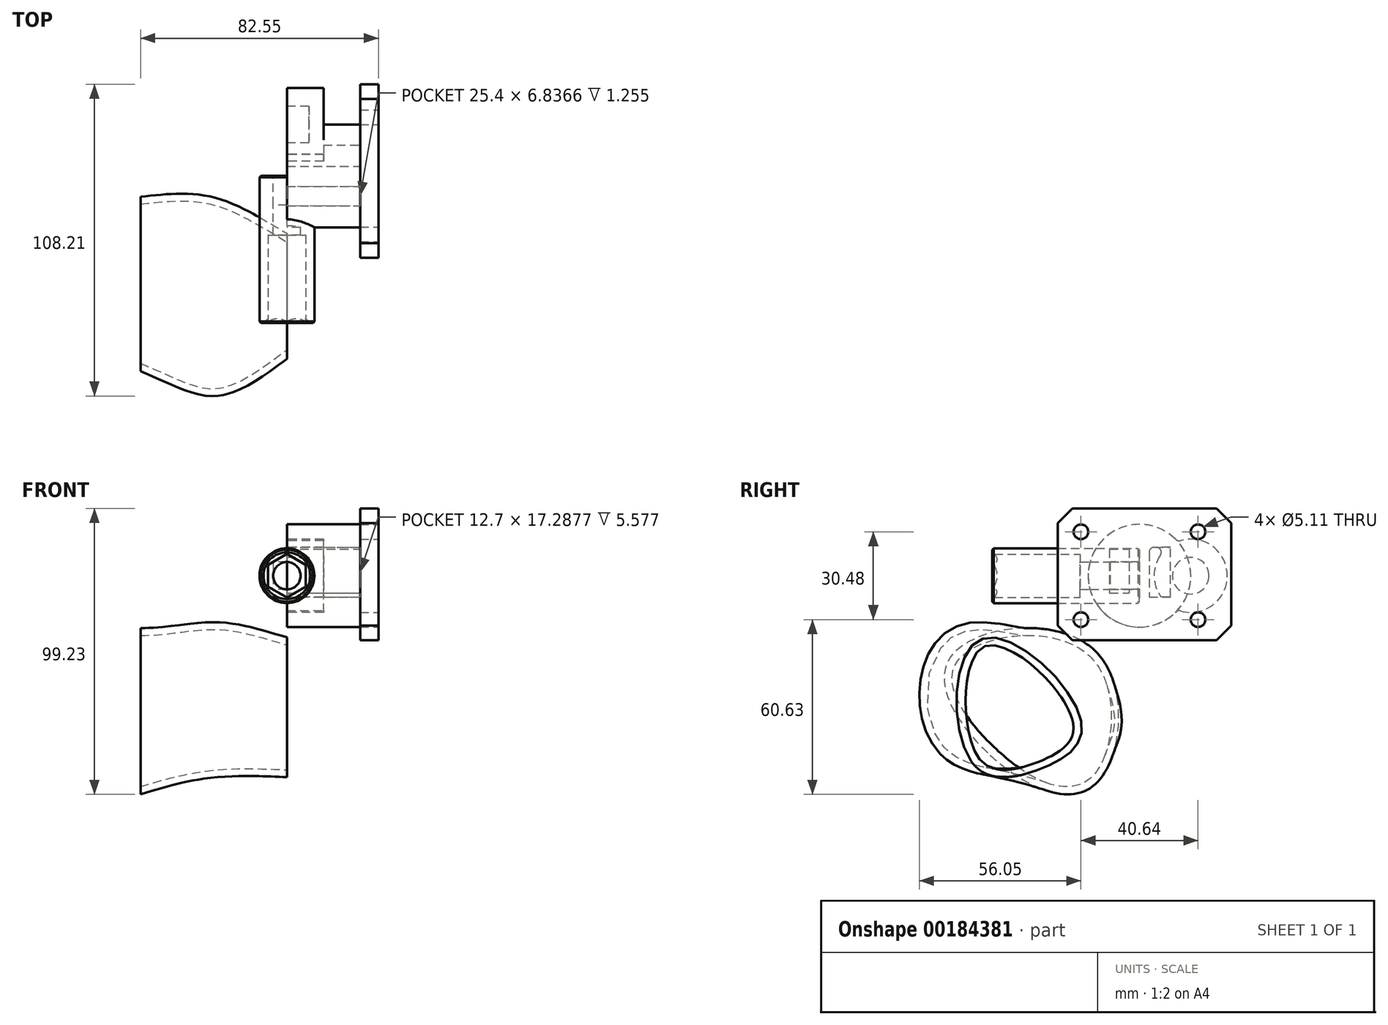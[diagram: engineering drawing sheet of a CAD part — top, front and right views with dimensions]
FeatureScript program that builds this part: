
annotation { "Feature Type Name" : "Feature", "Feature Type Description" : "" }
export const myFeature = defineFeature(function(context is Context, id is Id, definition is map)
    precondition{}
    {
        {
            var Q0;
            Q0=qCreatedBy(makeId("Front.planeOp"),FACE);
            var sketch = newSketch(context, id + "F0", { "sketchPlane" : qUnion([Q0])});
            skCircle(sketch, "E0", {"center": v(0, 0) * mm, "radius": 9.53 * mm});
            skSolve(sketch);
        }
        {
            var Q0;
            Q0 = qSketchRegion(id + "F0", true);
            extrude(context, id + "F1", {"entities" : qUnion([Q0]), "depth" : 51.05 * mm});
        }
        {
            var Q0;
            Q0=qCreatedBy(makeId("Front.planeOp"),FACE);
            var sketch = newSketch(context, id + "F2", { "sketchPlane" : qUnion([Q0])});
            skLineSegment(sketch, "E1.bottom", {"start": v(4.76, 4.76) * mm, "end": v(-4.76, 4.76) * mm});
            skLineSegment(sketch, "E1.top", {"start": v(4.76, -4.76) * mm, "end": v(-4.76, -4.76) * mm});
            skLineSegment(sketch, "E1.left", {"start": v(4.76, 4.76) * mm, "end": v(4.76, -4.76) * mm});
            skLineSegment(sketch, "E1.right", {"start": v(-4.76, 4.76) * mm, "end": v(-4.76, -4.76) * mm});
            skPoint(sketch, "E1.middle", {"position": v(0, 0) * mm});
            skCircle(sketch, "E2", {"center": v(0, 0) * mm, "radius": 4.76 * mm});
            skSolve(sketch);
        }
        {
            var Q0;
            {var subQ0=sQuery(id+"F2.wireOp",EDGE,"E2");var subQ1=makeQuery(id+"F2.imprint","INTERSECT",VERTEX,{"derivedFrom":[sQuery(id+"F2.wireOp",EDGE,"E1.bottom"),subQ0]});Q0=makeQuery(id+"F2.imprint","IMPRINT",FACE,{"disambiguationData":[TD([[makeQuery(id+"F2.imprint","IMPRINT",EDGE,{"disambiguationData":[TD([[subQ1,1.0]])],"derivedFrom":subQ0}),1.0]])]});}
            extrude(context, id + "F3", {"entities" : qUnion([Q0]), "operationType" : NewBodyOperationType.REMOVE, "endBound" : BoundingType.THROUGH_ALL, "depth" : 25.4 * mm});
        }
        {
            var Q0;
            Q0 = qSketchRegion(id + "F2", true);
            extrude(context, id + "F4", {"entities" : qUnion([Q0]), "operationType" : NewBodyOperationType.REMOVE, "depth" : 10.16 * mm});
        }
        {
            var Q0;
            Q0=makeQuery(id+"F1.opExtrude","CAP_FACE",FACE,{"disambiguationData":[OSD([sQuery(id+"F0.wireOp",EDGE,"E0")])],"isStart":false});
            var sketch = newSketch(context, id + "F5", { "sketchPlane" : qUnion([Q0])});
            skCircle(sketch, "E3.cCircle", {"center": v(0, 0) * mm, "radius": 6.54 * mm, "construction": true});
            skLineSegment(sketch, "E3.0", {"start": v(6.54, 3.78) * mm, "end": v(6.54, -3.78) * mm});
            skLineSegment(sketch, "E3.1", {"start": v(6.54, -3.78) * mm, "end": v(0, -7.55) * mm});
            skLineSegment(sketch, "E3.2", {"start": v(0, -7.55) * mm, "end": v(-6.54, -3.78) * mm});
            skLineSegment(sketch, "E3.3", {"start": v(-6.54, -3.78) * mm, "end": v(-6.54, 3.78) * mm});
            skLineSegment(sketch, "E3.4", {"start": v(-6.54, 3.78) * mm, "end": v(0, 7.55) * mm});
            skLineSegment(sketch, "E3.5", {"start": v(0, 7.55) * mm, "end": v(6.54, 3.78) * mm});
            skPoint(sketch, "E3.0.midPoint", {"position": v(6.54, 0) * mm});
            skSolve(sketch);
        }
        {
            var Q0;
            Q0 = qSketchRegion(id + "F5", true);
            extrude(context, id + "F6", {"entities" : qUnion([Q0]), "operationType" : NewBodyOperationType.REMOVE, "oppositeDirection" : true, "depth" : 30.48 * mm});
        }
        {
            var Q0;
            Q0=makeQuery(id+"F6.boolean.opBoolean","COPY",EDGE,{"derivedFrom":makeQuery(id+"F6.opExtrude","SWEPT_EDGE",EDGE,{"disambiguationData":[OSD([sQuery(id+"F5.wireOp",EDGE,"E3.4"),sQuery(id+"F5.wireOp",EDGE,"E3.5")])]})});
            var Q1;
            Q1=makeQuery(id+"F6.boolean.opBoolean","COPY",EDGE,{"derivedFrom":makeQuery(id+"F6.opExtrude","SWEPT_EDGE",EDGE,{"disambiguationData":[OSD([sQuery(id+"F5.wireOp",EDGE,"E3.3"),sQuery(id+"F5.wireOp",EDGE,"E3.4")])]})});
            var Q2;
            Q2=makeQuery(id+"F6.boolean.opBoolean","COPY",EDGE,{"derivedFrom":makeQuery(id+"F6.opExtrude","SWEPT_EDGE",EDGE,{"disambiguationData":[OSD([sQuery(id+"F5.wireOp",EDGE,"E3.2"),sQuery(id+"F5.wireOp",EDGE,"E3.3")])]})});
            var Q3;
            Q3=makeQuery(id+"F6.boolean.opBoolean","COPY",EDGE,{"derivedFrom":makeQuery(id+"F6.opExtrude","SWEPT_EDGE",EDGE,{"disambiguationData":[OSD([sQuery(id+"F5.wireOp",EDGE,"E3.1"),sQuery(id+"F5.wireOp",EDGE,"E3.2")])]})});
            var Q4;
            Q4=makeQuery(id+"F6.boolean.opBoolean","COPY",EDGE,{"derivedFrom":makeQuery(id+"F6.opExtrude","SWEPT_EDGE",EDGE,{"disambiguationData":[OSD([sQuery(id+"F5.wireOp",EDGE,"E3.0"),sQuery(id+"F5.wireOp",EDGE,"E3.1")])]})});
            var Q5;
            Q5=makeQuery(id+"F6.boolean.opBoolean","COPY",EDGE,{"derivedFrom":makeQuery(id+"F6.opExtrude","SWEPT_EDGE",EDGE,{"disambiguationData":[OSD([sQuery(id+"F5.wireOp",EDGE,"E3.0"),sQuery(id+"F5.wireOp",EDGE,"E3.5")])]})});
            fillet(context, id + "F7", {"entities" : qUnion([Q0, Q1, Q2, Q3, Q4, Q5]), "radius" : 0.5 * mm, "tangentPropagation" : true, "allowEdgeOverflow" : false});
        }
        {
            var Q0;
            Q0=qCreatedBy(makeId("Right.planeOp"),FACE);
            var sketch = newSketch(context, id + "F8", { "sketchPlane" : qUnion([Q0])});
            skLineSegment(sketch, "E4", {"start": v(0, 0) * mm, "end": v(-83.35, 0) * mm, "construction": true});
            skLineSegment(sketch, "E5", {"start": v(-51.05, 8.13) * mm, "end": v(-42.93, 0) * mm});
            skLineSegment(sketch, "E6", {"start": v(-42.93, 0) * mm, "end": v(-51.05, 0) * mm});
            skLineSegment(sketch, "E7", {"start": v(-51.05, 0) * mm, "end": v(-51.05, 8.13) * mm});
            skSolve(sketch);
        }
        {
            var Q0;
            Q0=makeQuery(id+"F8.imprint","IMPRINT",FACE,{"disambiguationData":[TD([[makeQuery(id+"F8.imprint","IMPRINT",EDGE,{"derivedFrom":sQuery(id+"F8.wireOp",EDGE,"E5")}),-1.0]])]});
            var Q1;
            Q1=sQuery(id+"F8.wireOp",EDGE,"E4");
            revolve(context, id + "F9", {"operationType" : NewBodyOperationType.REMOVE, "entities" : qUnion([Q0]), "axis" : qUnion([Q1]), "revolveType" : RevolveType.FULL, "oppositeDirection" : true});
        }
        {
            var Q0;
            Q0=makeQuery(id+"F1.opExtrude","CAP_EDGE",EDGE,{"disambiguationData":[OSD([sQuery(id+"F0.wireOp",EDGE,"E0")])],"isStart":false});
            var Q1;
            Q1=makeQuery(id+"F1.opExtrude","CAP_EDGE",EDGE,{"disambiguationData":[OSD([sQuery(id+"F0.wireOp",EDGE,"E0")])],"isStart":true});
            chamfer(context, id + "F10", {"entities" : qUnion([Q0, Q1]), "width" : 0.5 * mm, "tangentPropagation" : true});
        }
        {
            var Q0;
            Q0=qCreatedBy(makeId("Right.planeOp"),FACE);
            var sketch = newSketch(context, id + "F11", { "sketchPlane" : qUnion([Q0])});
            skCircle(sketch, "E8", {"center": v(0, 0) * mm, "radius": 17.82 * mm});
            skSolve(sketch);
        }
        {
            var Q0;
            Q0 = qSketchRegion(id + "F11", true);
            extrude(context, id + "F12", {"entities" : qUnion([Q0]), "operationType" : NewBodyOperationType.ADD, "depth" : 25.4 * mm});
        }
        {
            var Q0;
            Q0=makeQuery(id+"F12.opExtrude","CAP_FACE",FACE,{"disambiguationData":[OSD([sQuery(id+"F11.wireOp",EDGE,"E8")])],"isStart":false});
            var sketch = newSketch(context, id + "F13", { "sketchPlane" : qUnion([Q0])});
            skLineSegment(sketch, "E9.bottom", {"start": v(-10.41, 9.23) * mm, "end": v(-3.58, 9.23) * mm});
            skLineSegment(sketch, "E9.top", {"start": v(-10.41, -6.02) * mm, "end": v(-3.58, -6.02) * mm});
            skLineSegment(sketch, "E9.left", {"start": v(-10.41, 9.23) * mm, "end": v(-10.41, -6.02) * mm});
            skLineSegment(sketch, "E9.right", {"start": v(-3.58, 9.23) * mm, "end": v(-3.58, -6.02) * mm});
            skLineSegment(sketch, "E10.bottom", {"start": v(3.37, 9.89) * mm, "end": v(10.73, 9.89) * mm});
            skLineSegment(sketch, "E10.top", {"start": v(3.37, -7.4) * mm, "end": v(10.73, -7.4) * mm});
            skLineSegment(sketch, "E10.left", {"start": v(3.37, 9.89) * mm, "end": v(3.37, -7.4) * mm});
            skLineSegment(sketch, "E10.right", {"start": v(10.73, 9.89) * mm, "end": v(10.73, -7.4) * mm});
            skSolve(sketch);
        }
        {
            var Q0;
            Q0 = qSketchRegion(id + "F13", true);
            extrude(context, id + "F14", {"entities" : qUnion([Q0]), "operationType" : NewBodyOperationType.REMOVE, "oppositeDirection" : true, "depth" : 25.4 * mm});
        }
        {
            var Q0;
            Q0=makeQuery(id+"F12.opExtrude","CAP_FACE",FACE,{"disambiguationData":[OSD([sQuery(id+"F11.wireOp",EDGE,"E8")])],"isStart":false});
            var sketch = newSketch(context, id + "F15", { "sketchPlane" : qUnion([Q0])});
            skLineSegment(sketch, "E11.bottom", {"start": v(-28.4, 23.36) * mm, "end": v(31.84, 23.36) * mm});
            skLineSegment(sketch, "E11.top", {"start": v(-28.4, -22.4) * mm, "end": v(31.84, -22.4) * mm});
            skLineSegment(sketch, "E11.left", {"start": v(-28.4, 23.36) * mm, "end": v(-28.4, -22.4) * mm});
            skLineSegment(sketch, "E11.right", {"start": v(31.84, 23.36) * mm, "end": v(31.84, -22.4) * mm});
            skSolve(sketch);
        }
        {
            var Q0;
            Q0 = qSketchRegion(id + "F15", true);
            extrude(context, id + "F16", {"entities" : qUnion([Q0]), "operationType" : NewBodyOperationType.ADD, "depth" : 6.35 * mm});
        }
        {
            var Q0;
            Q0=qCreatedBy(makeId("Right.planeOp"),FACE);
            var sketch = newSketch(context, id + "F17", { "sketchPlane" : qUnion([Q0])});
            skCircle(sketch, "E12", {"center": v(17.78, 0) * mm, "radius": 12.7 * mm});
            skSolve(sketch);
        }
        {
            var Q0;
            Q0 = qSketchRegion(id + "F17", true);
            extrude(context, id + "F18", {"entities" : qUnion([Q0]), "operationType" : NewBodyOperationType.ADD, "depth" : 12.7 * mm});
        }
        {
            var Q0;
            Q0=makeQuery(id+"F16.opExtrude","SWEPT_EDGE",EDGE,{"disambiguationData":[OSD([sQuery(id+"F15.wireOp",EDGE,"E11.top"),sQuery(id+"F15.wireOp",EDGE,"E11.right")])]});
            var Q1;
            Q1=makeQuery(id+"F16.opExtrude","SWEPT_EDGE",EDGE,{"disambiguationData":[OSD([sQuery(id+"F15.wireOp",EDGE,"E11.top"),sQuery(id+"F15.wireOp",EDGE,"E11.left")])]});
            var Q2;
            Q2=makeQuery(id+"F16.opExtrude","SWEPT_EDGE",EDGE,{"disambiguationData":[OSD([sQuery(id+"F15.wireOp",EDGE,"E11.bottom"),sQuery(id+"F15.wireOp",EDGE,"E11.left")])]});
            var Q3;
            Q3=makeQuery(id+"F16.opExtrude","SWEPT_EDGE",EDGE,{"disambiguationData":[OSD([sQuery(id+"F15.wireOp",EDGE,"E11.bottom"),sQuery(id+"F15.wireOp",EDGE,"E11.right")])]});
            chamfer(context, id + "F19", {"entities" : qUnion([Q0, Q1, Q2, Q3]), "width" : 5.08 * mm, "tangentPropagation" : true});
        }
        {
            var Q0;
            Q0=makeQuery(id+"F16.opExtrude","CAP_FACE",FACE,{"disambiguationData":[OSD([sQuery(id+"F15.wireOp",EDGE,"E11.bottom"),sQuery(id+"F15.wireOp",EDGE,"E11.top"),sQuery(id+"F15.wireOp",EDGE,"E11.left"),sQuery(id+"F15.wireOp",EDGE,"E11.right")])],"isStart":false});
            var sketch = newSketch(context, id + "F20", { "sketchPlane" : qUnion([Q0])});
            skCircle(sketch, "E13", {"center": v(-20.32, -15.24) * mm, "radius": 2.55 * mm});
            skLineSegment(sketch, "E14", {"start": v(0, 0) * mm, "end": v(-58.83, 0) * mm, "construction": true});
            skCircle(sketch, "E15.MirrorC", {"center": v(-20.32, 15.24) * mm, "radius": 2.55 * mm});
            skLineSegment(sketch, "E16", {"start": v(0, 0) * mm, "end": v(0, -86.74) * mm, "construction": true});
            skCircle(sketch, "E17.MirrorC", {"center": v(20.32, 15.24) * mm, "radius": 2.55 * mm});
            skCircle(sketch, "E18.MirrorC", {"center": v(20.32, -15.24) * mm, "radius": 2.55 * mm});
            skSolve(sketch);
        }
        {
            var Q0;
            Q0 = qSketchRegion(id + "F20", true);
            extrude(context, id + "F21", {"entities" : qUnion([Q0]), "operationType" : NewBodyOperationType.REMOVE, "oppositeDirection" : true, "depth" : 12.7 * mm});
        }
        {
            var Q0;
            Q0=qCreatedBy(makeId("Right.planeOp"),FACE);
            var sketch = newSketch(context, id + "F22", { "sketchPlane" : qUnion([Q0])});
            skFitSpline(sketch, "E19", {"points": [v(-58.52, -64.24) * mm, v(-33.89, -66.86) * mm, v(-20.22, -50.28) * mm, v(-54.96, -22.02) * mm, v(-58.52, -64.24) * mm]});
            skSolve(sketch);
        }
        {
            var Q0;
            Q0=qCreatedBy(makeId("Right.planeOp"),FACE);
            cPlane(context, id + "F23", {"entities" : qUnion([Q0]), "cplaneType" : CPlaneType.OFFSET, "offset" : 25.4 * mm, "oppositeDirection" : true, "width" : 152.4 * mm, "height" : 152.4 * mm});
        }
        {
            var Q0;
            Q0=qCreatedBy(id+"F23.planeOp",FACE);
            var sketch = newSketch(context, id + "F24", { "sketchPlane" : qUnion([Q0])});
            skFitSpline(sketch, "E20", {"points": [v(-12.92, -61.32) * mm, v(-13.1, -37.85) * mm, v(-65.5, -18.56) * mm, v(-68.96, -61.68) * mm, v(-12.92, -61.32) * mm]});
            skSolve(sketch);
        }
        {
            var Q0;
            Q0=qCreatedBy(id+"F23.planeOp",FACE);
            cPlane(context, id + "F25", {"entities" : qUnion([Q0]), "cplaneType" : CPlaneType.OFFSET, "offset" : 25.4 * mm, "oppositeDirection" : true, "width" : 152.4 * mm, "height" : 152.4 * mm});
        }
        {
            var Q0;
            Q0=qCreatedBy(id+"F25.planeOp",FACE);
            var sketch = newSketch(context, id + "F26", { "sketchPlane" : qUnion([Q0])});
            skFitSpline(sketch, "E21", {"points": [v(-15.83, -72.78) * mm, v(-15.65, -25.84) * mm, v(-65.32, -27.84) * mm, v(-51.86, -62.23) * mm, v(-15.83, -72.78) * mm]});
            skSolve(sketch);
        }
        {
            var Q0;
            Q0=makeQuery(id+"F22.imprint","IMPRINT",FACE,{"disambiguationData":[TD([[makeQuery(id+"F22.imprint","IMPRINT",EDGE,{"derivedFrom":sQuery(id+"F22.wireOp",EDGE,"E19")}),1.0]])]});
            var Q1;
            Q1=makeQuery(id+"F24.imprint","IMPRINT",FACE,{"disambiguationData":[TD([[makeQuery(id+"F24.imprint","IMPRINT",EDGE,{"derivedFrom":sQuery(id+"F24.wireOp",EDGE,"E20")}),1.0]])]});
            var Q2;
            Q2=makeQuery(id+"F26.imprint","IMPRINT",FACE,{"disambiguationData":[TD([[makeQuery(id+"F26.imprint","IMPRINT",EDGE,{"derivedFrom":sQuery(id+"F26.wireOp",EDGE,"E21")}),1.0]])]});
            var Q3;
            Q3=sQuery(id+"F22.wireOp",VERTEX,"E19.0.internal");
            var Q4;
            Q4=sQuery(id+"F24.wireOp",VERTEX,"E20.3.internal");
            var Q5;
            Q5=sQuery(id+"F26.wireOp",VERTEX,"E21.3.internal");
            loft(context, id + "F27", {"sheetProfilesArray" : [{ "sheetProfileEntities" : qUnion([Q0]) }, { "sheetProfileEntities" : qUnion([Q1]) }, { "sheetProfileEntities" : qUnion([Q2]) }], "matchConnections" : true, "connections" : [{ "connectionEntities" : qUnion([Q3, Q4, Q5]), "connectionEdgeQueries" : qUnion([]), "connectionEdgeParameters" : [] }]});
        }
        {
            var Q0;
            {var subQ1=sQuery(id+"F11.wireOp",EDGE,"E8");var subQ2=sQuery(id+"F0.wireOp",EDGE,"E0");Q0=makeQuery(id+"F18.boolean.opBoolean","MERGE",FACE,{"derivedFrom":[makeQuery(id+"F14.boolean.opBoolean","SPLIT",FACE,{"disambiguationData":[TD([makeQuery(id+"F1.opExtrude","SWEPT_FACE",FACE,{"disambiguationData":[OSD([subQ2])]})])],"derivedFrom":makeQuery(id+"F12.opExtrude","CAP_FACE",FACE,{"disambiguationData":[OSD([subQ1])],"isStart":true})}),makeQuery(id+"F18.opExtrude","CAP_FACE",FACE,{"disambiguationData":[OSD([sQuery(id+"F17.wireOp",EDGE,"E12")])],"isStart":true})]});}
            var sketch = newSketch(context, id + "F28", { "sketchPlane" : qUnion([Q0])});
            skCircle(sketch, "E22", {"center": v(-17.78, 0) * mm, "radius": 6.35 * mm});
            skSolve(sketch);
        }
        {
            var Q0;
            Q0 = qSketchRegion(id + "F28", true);
            extrude(context, id + "F29", {"entities" : qUnion([Q0]), "operationType" : NewBodyOperationType.REMOVE, "oppositeDirection" : true, "depth" : 7.62 * mm});
        }
        {
            var Q0;
            {var subQ0=sQuery(id+"F11.wireOp",EDGE,"E8");Q0=makeQuery(id+"F18.boolean.opBoolean","INTERSECT",EDGE,{"disambiguationData":[OD(1.0)],"derivedFrom":[makeQuery(id+"F12.boolean.opBoolean","SPLIT",FACE,{"disambiguationData":[TD([makeQuery(id+"F1.opExtrude","SWEPT_FACE",FACE,{"disambiguationData":[OSD([sQuery(id+"F0.wireOp",EDGE,"E0")])]})])],"derivedFrom":makeQuery(id+"F12.opExtrude","SWEPT_FACE",FACE,{"disambiguationData":[OSD([subQ0])]})}),makeQuery(id+"F18.opExtrude","SWEPT_FACE",FACE,{"disambiguationData":[OSD([sQuery(id+"F17.wireOp",EDGE,"E12")])]})]});}
            var Q1;
            {var subQ0=sQuery(id+"F11.wireOp",EDGE,"E8");Q1=makeQuery(id+"F18.boolean.opBoolean","INTERSECT",EDGE,{"disambiguationData":[OD(0.0)],"derivedFrom":[makeQuery(id+"F12.boolean.opBoolean","SPLIT",FACE,{"disambiguationData":[TD([makeQuery(id+"F1.opExtrude","SWEPT_FACE",FACE,{"disambiguationData":[OSD([sQuery(id+"F0.wireOp",EDGE,"E0")])]})])],"derivedFrom":makeQuery(id+"F12.opExtrude","SWEPT_FACE",FACE,{"disambiguationData":[OSD([subQ0])]})}),makeQuery(id+"F18.opExtrude","SWEPT_FACE",FACE,{"disambiguationData":[OSD([sQuery(id+"F17.wireOp",EDGE,"E12")])]})]});}
            var Q2;
            Q2=makeQuery(id+"F14.boolean.opBoolean","COPY",EDGE,{"derivedFrom":makeQuery(id+"F14.opExtrude","SWEPT_EDGE",EDGE,{"disambiguationData":[OSD([sQuery(id+"F13.wireOp",EDGE,"E10.bottom"),sQuery(id+"F13.wireOp",EDGE,"E10.left")])]})});
            var Q3;
            Q3=makeQuery(id+"F18.boolean.opBoolean","INTERSECT",EDGE,{"derivedFrom":[makeQuery(id+"F14.boolean.opBoolean","COPY",FACE,{"derivedFrom":makeQuery(id+"F14.opExtrude","SWEPT_FACE",FACE,{"disambiguationData":[OSD([sQuery(id+"F13.wireOp",EDGE,"E10.bottom")])]})}),makeQuery(id+"F18.opExtrude","SWEPT_FACE",FACE,{"disambiguationData":[OSD([sQuery(id+"F17.wireOp",EDGE,"E12")])]})]});
            fillet(context, id + "F30", {"entities" : qUnion([Q0, Q1, Q2, Q3]), "radius" : 1.78 * mm, "allowEdgeOverflow" : false});
        }
        {
            var Q0;
            Q0=makeQuery(id+"F27.opLoft","CAP_FACE",FACE,{"disambiguationData":[OSD([makeQuery(id+"F26.imprint","IMPRINT",FACE,{"disambiguationData":[TD([[makeQuery(id+"F26.imprint","IMPRINT",EDGE,{"derivedFrom":sQuery(id+"F26.wireOp",EDGE,"E21")}),1.0]])]})])],"isStart":true});
            var Q1;
            Q1=makeQuery(id+"F27.opLoft","CAP_FACE",FACE,{"disambiguationData":[OSD([makeQuery(id+"F22.imprint","IMPRINT",FACE,{"disambiguationData":[TD([[makeQuery(id+"F22.imprint","IMPRINT",EDGE,{"derivedFrom":sQuery(id+"F22.wireOp",EDGE,"E19")}),1.0]])]})])],"isStart":true});
            shell(context, id + "F31", {"entities" : qUnion([Q0, Q1]), "thickness" : 2.54 * mm});
        }
    });
